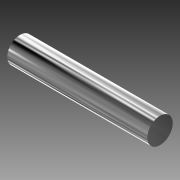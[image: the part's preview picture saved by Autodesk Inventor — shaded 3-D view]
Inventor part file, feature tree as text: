
AUTODESK INVENTOR PART (.ipt)
format: ipt  version: 2012 (Build 160160000, 160)  size: 71,680 bytes
history: native  units: mm
features: extrude x1, sketch x1
ambient origin geometry x8: Origin, YZ Plane, XZ Plane, XY Plane, X Axis, Y Axis, Z Axis, Center Point
bodies: Solid1 (feature_tree)
feature tree (2):
  extrude  "Extrusion1"  Depth=44.0mm TaperAngle=0.0deg
  sketch  "Sketch2"  dims[d0=8.0mm d2=44.0mm d3=0.0mm]
